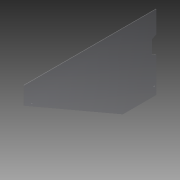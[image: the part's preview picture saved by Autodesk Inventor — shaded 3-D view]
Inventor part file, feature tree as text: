
AUTODESK INVENTOR PART (.ipt)
format: ipt  version: 2015 SP1 (Build 190203100, 203)  size: 123,392 bytes
history: native  units: in
note: dims shown in document units (in); Inventor stores cm internally (conversion verified against a paired STEP export)
features: sketch x2, extrude x1, hole x1, projected_geometry x1
ambient origin geometry x8: Origin, YZ Plane, XZ Plane, XY Plane, X Axis, Y Axis, Z Axis, Center Point
bodies: Solid1 (feature_tree)
feature tree (5):
  extrude  "Extrusion1"  TaperAngle=180.0deg  [1 undecoded]
  hole  "Hole1"  [1 undecoded]
  sketch  "Sketch1"  dims[d0=5.0in d1=180.0deg]
  sketch  "Sketch2"  dims[d8=7.922in d10=30.0in d11=90.0deg d13=90.0deg d14=90.0deg d16=0.125in d17=0.0in d18=112.5deg d19=3.125in d20=112.5deg d21=112.5deg d22=1.0in d23=0.0in d24=4.375in d25=1.75in d26=2.0in d27=0.5in d28=0.25in d29=0.75in d30=0.375in d31=0.25in d32=0.5635in d33=1.0in d34=0.8108in d35=4.0in d36=7.625in]
  projected_geometry  "Projected Loop1"
note: 2 required parameter values undecoded (feature->parameter linkage not recoverable at this tier; creation-order binding heuristic only, values carry confidence <= 0.55)
